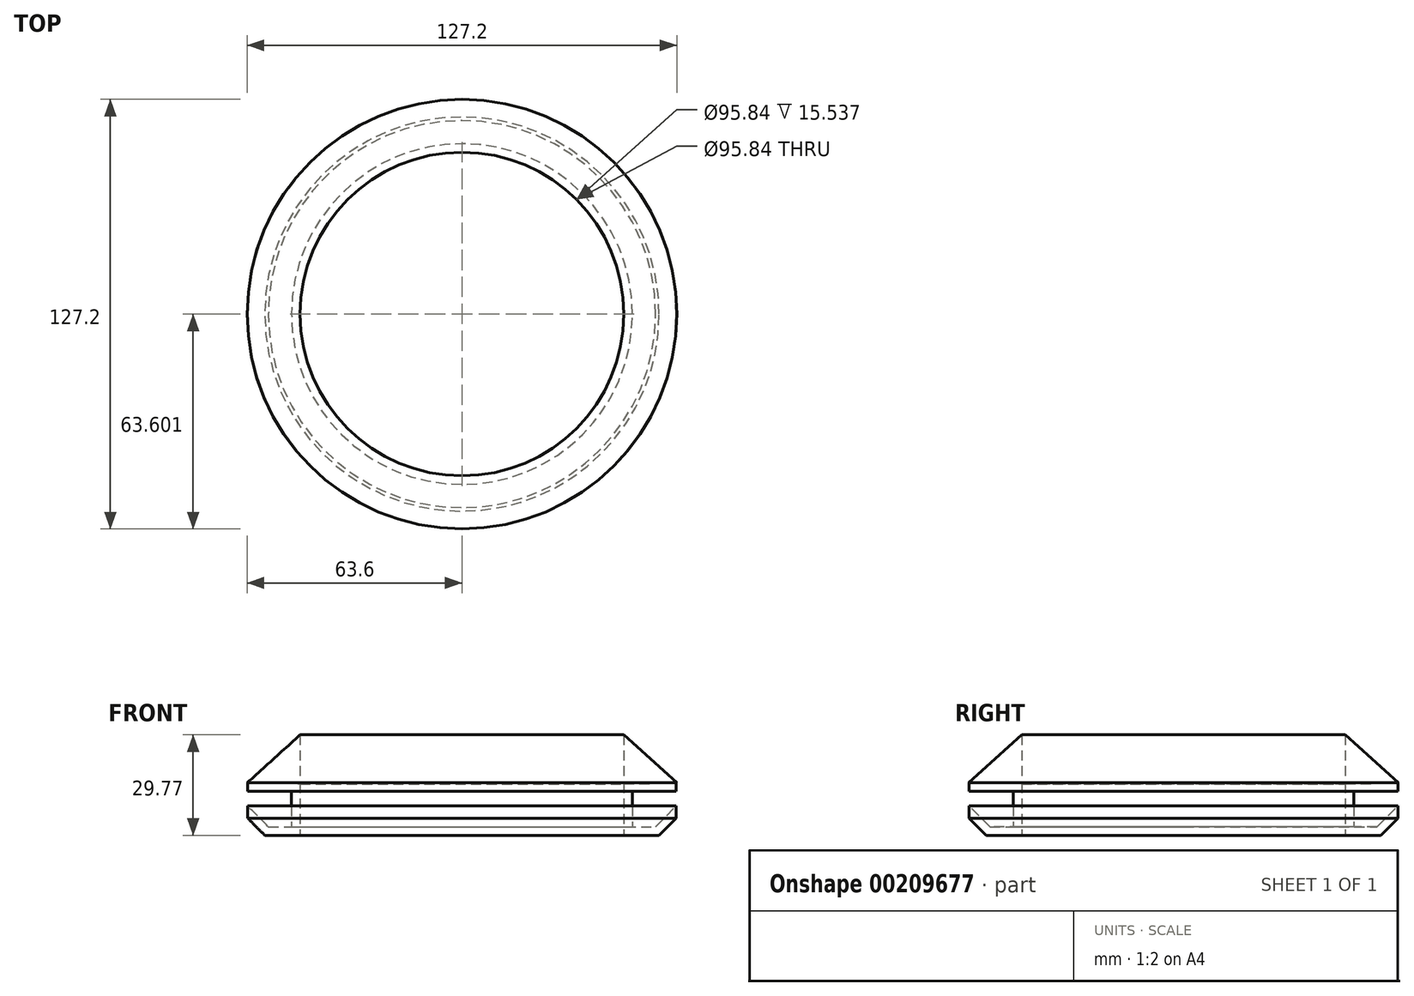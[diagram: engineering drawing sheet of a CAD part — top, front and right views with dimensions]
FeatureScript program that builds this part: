
annotation { "Feature Type Name" : "Feature", "Feature Type Description" : "" }
export const myFeature = defineFeature(function(context is Context, id is Id, definition is map)
    precondition{}
    {
        {
            var Q0;
            Q0=qCreatedBy(makeId("Right.planeOp"),FACE);
            var sketch = newSketch(context, id + "F0", { "sketchPlane" : qUnion([Q0])});
            skLineSegment(sketch, "E0.bottom", {"start": v(0, 15.54) * mm, "end": v(15.54, 15.54) * mm});
            skLineSegment(sketch, "E0.top", {"start": v(0, 0) * mm, "end": v(15.54, 0) * mm});
            skLineSegment(sketch, "E0.left", {"start": v(0, 15.54) * mm, "end": v(0, 0) * mm});
            skLineSegment(sketch, "E0.right", {"start": v(15.54, 15.54) * mm, "end": v(15.54, 0) * mm});
            skSolve(sketch);
        }
        {
            var Q0;
            Q0=qCreatedBy(makeId("Right.planeOp"),FACE);
            var sketch = newSketch(context, id + "F1", { "sketchPlane" : qUnion([Q0])});
            skLineSegment(sketch, "E1", {"start": v(15.68, 15.54) * mm, "end": v(0, 29.77) * mm});
            skLineSegment(sketch, "E2", {"start": v(0, 29.77) * mm, "end": v(0, 15.25) * mm});
            skLineSegment(sketch, "E3", {"start": v(0, 15.25) * mm, "end": v(15.68, 15.54) * mm});
            skLineSegment(sketch, "E4", {"start": v(0, 0) * mm, "end": v(0, 70.14) * mm, "construction": true});
            skLineSegment(sketch, "E5", {"start": v(-47.92, 0) * mm, "end": v(-47.92, 71.3) * mm, "construction": true});
            skSolve(sketch);
        }
        {
            var Q0;
            Q0=makeQuery(id+"F1.imprint","IMPRINT",FACE,{"disambiguationData":[TD([[makeQuery(id+"F1.imprint","IMPRINT",EDGE,{"derivedFrom":sQuery(id+"F1.wireOp",EDGE,"E1")}),1.0]])]});
            var Q1;
            Q1=makeQuery(id+"F0.imprint","IMPRINT",FACE,{"disambiguationData":[TD([[makeQuery(id+"F0.imprint","IMPRINT",EDGE,{"derivedFrom":sQuery(id+"F0.wireOp",EDGE,"E0.bottom")}),-1.0]])]});
            var Q2;
            Q2=sQuery(id+"F1.wireOp",EDGE,"E5");
            revolve(context, id + "F2", {"entities" : qUnion([Q0, Q1]), "axis" : qUnion([Q2]), "revolveType" : RevolveType.FULL});
        }
        {
            var Q0;
            Q0=makeQuery(id+"F2.opRevolve","SWEPT_EDGE",EDGE,{"disambiguationData":[OSD([sQuery(id+"F0.wireOp",EDGE,"E0.top"),sQuery(id+"F0.wireOp",EDGE,"E0.right")])]});
            chamfer(context, id + "F3", {"entities" : qUnion([Q0]), "width" : 5.08 * mm, "tangentPropagation" : true});
        }
        {
            var Q0;
            Q0=makeQuery(id+"F2.opRevolve","SWEPT_FACE",FACE,{"disambiguationData":[OSD([sQuery(id+"F0.wireOp",EDGE,"E0.right")])]});
            shell(context, id + "F4", {"entities" : qUnion([Q0]), "thickness" : 2.54 * mm});
        }
    });
